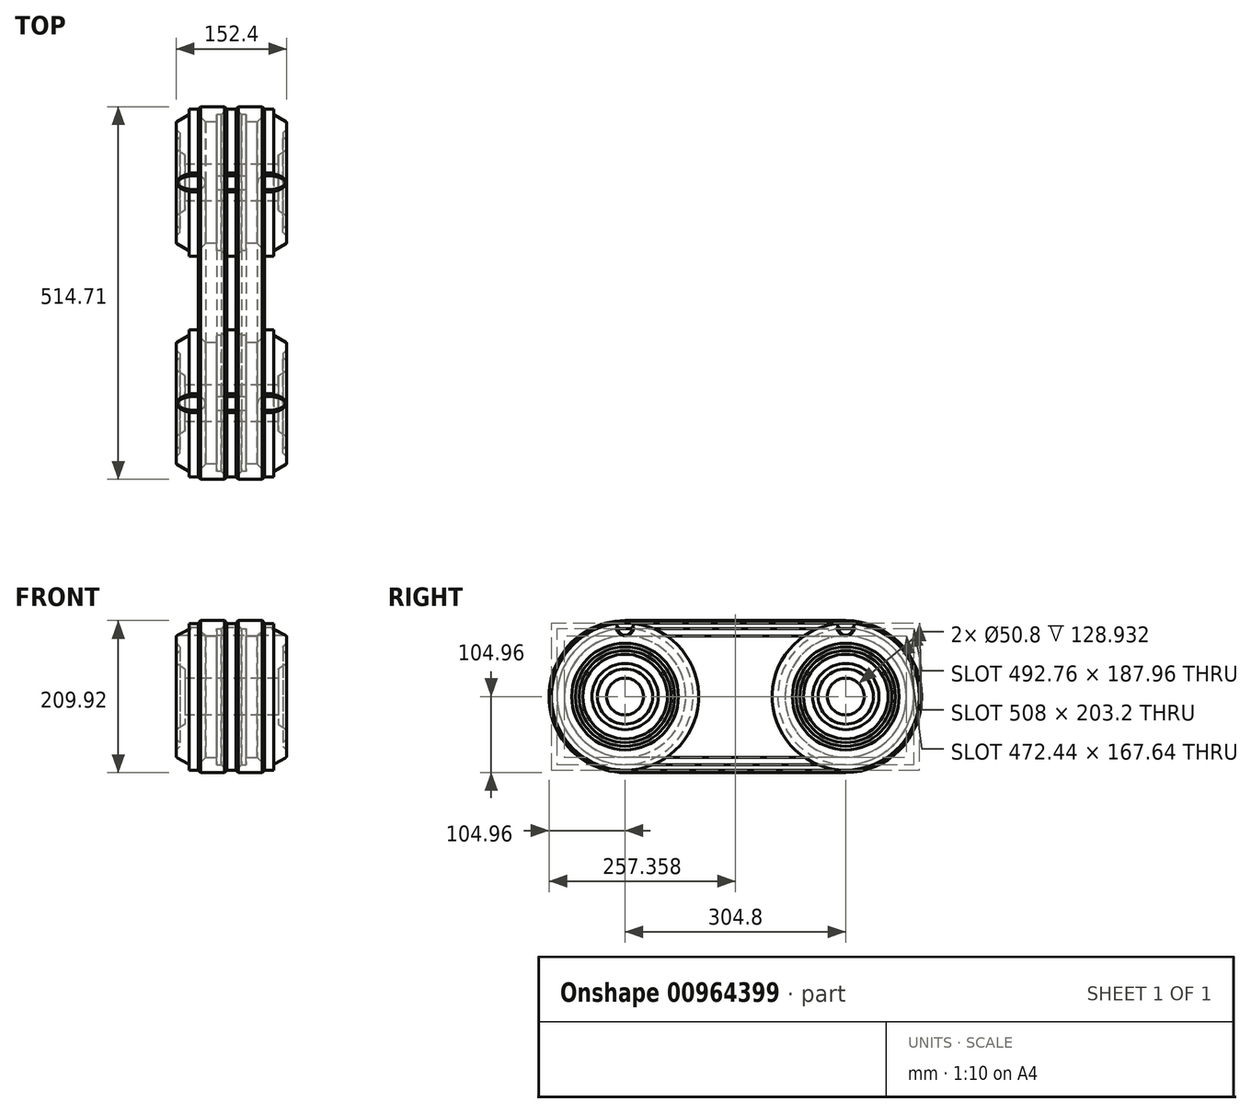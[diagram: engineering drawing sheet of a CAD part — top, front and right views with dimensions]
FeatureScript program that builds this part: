
annotation { "Feature Type Name" : "Feature", "Feature Type Description" : "" }
export const myFeature = defineFeature(function(context is Context, id is Id, definition is map)
    precondition{}
    {
        {
            var Q0;
            Q0=qCreatedBy(makeId("Top.planeOp"),FACE);
            var sketch = newSketch(context, id + "F0", { "sketchPlane" : qUnion([Q0])});
            skLineSegment(sketch, "E0", {"start": v(-162.42, 0) * mm, "end": v(162.97, 0) * mm, "construction": true});
            skLineSegment(sketch, "E1", {"start": v(0, 108.88) * mm, "end": v(0, -100.36) * mm, "construction": true});
            skLineSegment(sketch, "E2", {"start": v(-64.47, 25.4) * mm, "end": v(-64.47, 38.1) * mm});
            skLineSegment(sketch, "E3", {"start": v(-64.47, 38.1) * mm, "end": v(-76.2, 45.72) * mm});
            skLineSegment(sketch, "E4", {"start": v(-76.2, 45.72) * mm, "end": v(-76.2, 58.42) * mm});
            skLineSegment(sketch, "E5", {"start": v(-76.2, 58.42) * mm, "end": v(-71.12, 63.5) * mm});
            skLineSegment(sketch, "E6", {"start": v(-71.12, 63.5) * mm, "end": v(-71.12, 68.58) * mm});
            skLineSegment(sketch, "E7", {"start": v(-71.12, 68.58) * mm, "end": v(-76.2, 73.66) * mm});
            skLineSegment(sketch, "E8", {"start": v(-76.2, 73.66) * mm, "end": v(-76.2, 83.82) * mm});
            skLineSegment(sketch, "E9", {"start": v(-76.2, 83.82) * mm, "end": v(-58.42, 93.98) * mm});
            skLineSegment(sketch, "E10", {"start": v(-58.42, 93.98) * mm, "end": v(-58.42, 101.6) * mm});
            skLineSegment(sketch, "E11", {"start": v(-58.42, 101.6) * mm, "end": v(-45.72, 101.6) * mm});
            skLineSegment(sketch, "E12", {"start": v(-45.72, 101.6) * mm, "end": v(-45.72, 93.98) * mm});
            skLineSegment(sketch, "E13", {"start": v(-45.72, 93.98) * mm, "end": v(-35.56, 83.82) * mm});
            skLineSegment(sketch, "E14", {"start": v(-35.56, 83.82) * mm, "end": v(-20.32, 83.82) * mm});
            skLineSegment(sketch, "E15", {"start": v(-20.32, 83.82) * mm, "end": v(-20.32, 93.98) * mm});
            skLineSegment(sketch, "E16", {"start": v(-20.32, 93.98) * mm, "end": v(-13.97, 93.98) * mm});
            skLineSegment(sketch, "E17", {"start": v(-13.97, 93.98) * mm, "end": v(-6.35, 101.6) * mm});
            skLineSegment(sketch, "E18", {"start": v(-6.35, 101.6) * mm, "end": v(6.35, 101.6) * mm});
            skLineSegment(sketch, "E19", {"start": v(6.35, 101.6) * mm, "end": v(13.97, 93.98) * mm});
            skLineSegment(sketch, "E20", {"start": v(13.97, 93.98) * mm, "end": v(20.32, 93.98) * mm});
            skLineSegment(sketch, "E21", {"start": v(20.32, 93.98) * mm, "end": v(20.32, 83.82) * mm});
            skLineSegment(sketch, "E22", {"start": v(20.32, 83.82) * mm, "end": v(35.56, 83.82) * mm});
            skLineSegment(sketch, "E23", {"start": v(35.56, 83.82) * mm, "end": v(45.72, 93.98) * mm});
            skLineSegment(sketch, "E24", {"start": v(45.72, 93.98) * mm, "end": v(45.72, 101.6) * mm});
            skLineSegment(sketch, "E25", {"start": v(45.72, 101.6) * mm, "end": v(58.42, 101.6) * mm});
            skLineSegment(sketch, "E26", {"start": v(58.42, 101.6) * mm, "end": v(58.42, 93.98) * mm});
            skLineSegment(sketch, "E27", {"start": v(58.42, 93.98) * mm, "end": v(76.2, 83.82) * mm});
            skLineSegment(sketch, "E28", {"start": v(76.2, 83.82) * mm, "end": v(76.2, 73.66) * mm});
            skLineSegment(sketch, "E29", {"start": v(76.2, 73.66) * mm, "end": v(71.12, 68.58) * mm});
            skLineSegment(sketch, "E30", {"start": v(71.12, 68.58) * mm, "end": v(71.12, 63.5) * mm});
            skLineSegment(sketch, "E31", {"start": v(71.12, 63.5) * mm, "end": v(76.2, 58.42) * mm});
            skLineSegment(sketch, "E32", {"start": v(76.2, 58.42) * mm, "end": v(76.2, 45.72) * mm});
            skLineSegment(sketch, "E33", {"start": v(76.2, 45.72) * mm, "end": v(64.47, 38.1) * mm});
            skLineSegment(sketch, "E34", {"start": v(64.47, 38.1) * mm, "end": v(64.47, 25.4) * mm});
            skLineSegment(sketch, "E35", {"start": v(64.47, 25.4) * mm, "end": v(-64.47, 25.4) * mm});
            skSolve(sketch);
        }
        {
            var Q0;
            Q0=makeQuery(id+"F0.imprint","IMPRINT",FACE,{"disambiguationData":[TD([[makeQuery(id+"F0.imprint","IMPRINT",EDGE,{"derivedFrom":sQuery(id+"F0.wireOp",EDGE,"E2")}),-1.0]])]});
            var Q1;
            Q1=sQuery(id+"F0.wireOp",EDGE,"E0");
            revolve(context, id + "F1", {"surfaceOperationType" : NewSurfaceOperationType.NEW, "entities" : qUnion([Q0]), "axis" : qUnion([Q1]), "revolveType" : RevolveType.FULL});
        }
        {
            var Q0;
            Q0=qCreatedBy(makeId("Right.planeOp"),FACE);
            var sketch = newSketch(context, id + "F2", { "sketchPlane" : qUnion([Q0])});
            skCircle(sketch, "E36", {"center": v(0, 0) * mm, "radius": 94.18 * mm, "construction": true});
            skCircle(sketch, "E37", {"center": v(0, 94.18) * mm, "radius": 9.58 * mm});
            skLineSegment(sketch, "E38", {"start": v(9.51, 95.36) * mm, "end": v(16.3, 105.7) * mm});
            skLineSegment(sketch, "E39", {"start": v(16.3, 105.7) * mm, "end": v(-15.78, 105.7) * mm});
            skLineSegment(sketch, "E40", {"start": v(-15.78, 105.7) * mm, "end": v(-9.51, 95.36) * mm});
            skSolve(sketch);
        }
        {
            var Q0;
            Q0 = qSketchRegion(id + "F2", true);
            extrude(context, id + "F3", {"entities" : qUnion([Q0]), "operationType" : NewBodyOperationType.REMOVE, "endBound" : BoundingType.SYMMETRIC, "oppositeDirection" : true, "depth" : 254 * mm, "offsetDistance" : 25.4 * mm});
        }
        {
            var Q0;
            Q0=qCreatedBy(makeId("Top.planeOp"),FACE);
            var sketch = newSketch(context, id + "F4", { "sketchPlane" : qUnion([Q0])});
            skLineSegment(sketch, "E41", {"start": v(-162.42, 0) * mm, "end": v(162.97, 0) * mm, "construction": true});
            skLineSegment(sketch, "E42.MirrorCS", {"start": v(-6.35, -104.96) * mm, "end": v(-45.72, -104.96) * mm});
            skLineSegment(sketch, "E43.MirrorCS", {"start": v(6.35, -101.6) * mm, "end": v(6.35, -104.96) * mm});
            skLineSegment(sketch, "E44.MirrorCS", {"start": v(-6.35, -101.6) * mm, "end": v(-6.35, -104.96) * mm});
            skLineSegment(sketch, "E45.MirrorCS", {"start": v(-20.32, -93.98) * mm, "end": v(-13.97, -93.98) * mm});
            skLineSegment(sketch, "E46.MirrorCS", {"start": v(-45.72, -104.96) * mm, "end": v(-45.72, -101.6) * mm});
            skLineSegment(sketch, "E47.MirrorCS", {"start": v(13.97, -93.98) * mm, "end": v(20.32, -93.98) * mm});
            skLineSegment(sketch, "E48.MirrorCS", {"start": v(45.72, -104.96) * mm, "end": v(45.72, -101.6) * mm});
            skLineSegment(sketch, "E49.MirrorCS", {"start": v(45.72, -93.98) * mm, "end": v(45.72, -101.6) * mm});
            skLineSegment(sketch, "E50.MirrorCS", {"start": v(-45.72, -101.6) * mm, "end": v(-45.72, -93.98) * mm});
            skLineSegment(sketch, "E51.MirrorCS", {"start": v(20.32, -83.82) * mm, "end": v(35.56, -83.82) * mm});
            skLineSegment(sketch, "E52.MirrorCS", {"start": v(-45.72, -93.98) * mm, "end": v(-35.56, -83.82) * mm});
            skLineSegment(sketch, "E53.MirrorCS", {"start": v(-13.97, -93.98) * mm, "end": v(-6.35, -101.6) * mm});
            skLineSegment(sketch, "E54.MirrorCS", {"start": v(6.35, -101.6) * mm, "end": v(13.97, -93.98) * mm});
            skLineSegment(sketch, "E55.MirrorCS", {"start": v(35.56, -83.82) * mm, "end": v(45.72, -93.98) * mm});
            skLineSegment(sketch, "E56.MirrorCS", {"start": v(20.32, -93.98) * mm, "end": v(20.32, -83.82) * mm});
            skLineSegment(sketch, "E57.MirrorCS", {"start": v(-20.32, -83.82) * mm, "end": v(-20.32, -93.98) * mm});
            skLineSegment(sketch, "E58.MirrorCS", {"start": v(6.35, -104.96) * mm, "end": v(45.72, -104.96) * mm});
            skLineSegment(sketch, "E59.MirrorCS", {"start": v(-35.56, -83.82) * mm, "end": v(-20.32, -83.82) * mm});
            skLineSegment(sketch, "E60.MirrorCS", {"start": v(-6.35, -104.96) * mm, "end": v(6.35, -104.96) * mm, "construction": true});
            skSolve(sketch);
        }
        {
            var Q0;
            Q0=qCreatedBy(makeId("Right.planeOp"),FACE);
            var sketch = newSketch(context, id + "F5", { "sketchPlane" : qUnion([Q0])});
            skArc(sketch, "E61", {"start": v(304.8, -104.95) * mm, "mid": v(409.75, 0) * mm, "end": v(304.8, 104.95) * mm});
            skLineSegment(sketch, "E62", {"start": v(0, 104.96) * mm, "end": v(304.8, 104.95) * mm});
            skLineSegment(sketch, "E63", {"start": v(304.8, -104.95) * mm, "end": v(0, -104.96) * mm});
            skArc(sketch, "E64", {"start": v(0, 104.96) * mm, "mid": v(-104.96, 0) * mm, "end": v(0, -104.96) * mm});
            skLineSegment(sketch, "E65", {"start": v(0, 0) * mm, "end": v(304.8, 0) * mm, "construction": true});
            skSolve(sketch);
        }
        {
            var Q0;
            Q0=makeQuery(id+"F4.imprint","IMPRINT",FACE,{"disambiguationData":[TD([[makeQuery(id+"F4.imprint","IMPRINT",EDGE,{"derivedFrom":sQuery(id+"F4.wireOp",EDGE,"E43.MirrorCS")}),1.0]])]});
            var Q1;
            Q1=makeQuery(id+"F4.imprint","IMPRINT",FACE,{"disambiguationData":[TD([[makeQuery(id+"F4.imprint","IMPRINT",EDGE,{"derivedFrom":sQuery(id+"F4.wireOp",EDGE,"E44.MirrorCS")}),-1.0]])]});
            var Q2;
            Q2=sQuery(id+"F5.wireOp",EDGE,"E62");
            var Q3;
            Q3=sQuery(id+"F5.wireOp",EDGE,"E64");
            var Q4;
            Q4=sQuery(id+"F5.wireOp",EDGE,"E61");
            var Q5;
            Q5=sQuery(id+"F5.wireOp",EDGE,"E63");
            sweep(context, id + "F6", {"profiles" : qUnion([Q0, Q1]), "path" : qUnion([Q2, Q3, Q4, Q5])});
        }
        {
            var Q0;
            Q0=makeQuery(id+"F1.opRevolve","SWEPT_BODY",BODY,{"disambiguationData":[OSD([sQuery(id+"F0.wireOp",EDGE,"E2"),sQuery(id+"F0.wireOp",EDGE,"E3"),sQuery(id+"F0.wireOp",EDGE,"E4"),sQuery(id+"F0.wireOp",EDGE,"E5"),sQuery(id+"F0.wireOp",EDGE,"E6"),sQuery(id+"F0.wireOp",EDGE,"E7"),sQuery(id+"F0.wireOp",EDGE,"E8"),sQuery(id+"F0.wireOp",EDGE,"E9"),sQuery(id+"F0.wireOp",EDGE,"E10"),sQuery(id+"F0.wireOp",EDGE,"E11"),sQuery(id+"F0.wireOp",EDGE,"E12"),sQuery(id+"F0.wireOp",EDGE,"E13"),sQuery(id+"F0.wireOp",EDGE,"E14"),sQuery(id+"F0.wireOp",EDGE,"E15"),sQuery(id+"F0.wireOp",EDGE,"E16"),sQuery(id+"F0.wireOp",EDGE,"E17"),sQuery(id+"F0.wireOp",EDGE,"E18"),sQuery(id+"F0.wireOp",EDGE,"E19"),sQuery(id+"F0.wireOp",EDGE,"E20"),sQuery(id+"F0.wireOp",EDGE,"E21"),sQuery(id+"F0.wireOp",EDGE,"E22"),sQuery(id+"F0.wireOp",EDGE,"E23"),sQuery(id+"F0.wireOp",EDGE,"E24"),sQuery(id+"F0.wireOp",EDGE,"E25"),sQuery(id+"F0.wireOp",EDGE,"E26"),sQuery(id+"F0.wireOp",EDGE,"E27"),sQuery(id+"F0.wireOp",EDGE,"E28"),sQuery(id+"F0.wireOp",EDGE,"E29"),sQuery(id+"F0.wireOp",EDGE,"E30"),sQuery(id+"F0.wireOp",EDGE,"E31"),sQuery(id+"F0.wireOp",EDGE,"E32"),sQuery(id+"F0.wireOp",EDGE,"E33"),sQuery(id+"F0.wireOp",EDGE,"E34"),sQuery(id+"F0.wireOp",EDGE,"E35")])]});
            var Q1;
            Q1=sQuery(id+"F5.wireOp",EDGE,"E65");
            transform(context, id + "F7", {"entities" : qUnion([Q0]), "transformType" : TransformType.TRANSLATION_ENTITY, "oppositeDirectionEntity" : false, "transformLine" : qUnion([Q1]), "makeCopy" : true});
        }
        {
            var Q0;
            Q0=makeQuery(id+"F6.opSweep","SWEPT_EDGE",EDGE,{"disambiguationData":[OSD([sQuery(id+"F4.wireOp",EDGE,"E48.MirrorCS"),sQuery(id+"F4.wireOp",EDGE,"E58.MirrorCS"),sQuery(id+"F5.wireOp",EDGE,"E62")])]});
            var Q1;
            Q1=makeQuery(id+"F6.opSweep","SWEPT_FACE",FACE,{"disambiguationData":[OSD([sQuery(id+"F4.wireOp",EDGE,"E58.MirrorCS"),sQuery(id+"F5.wireOp",EDGE,"E62")])]});
            var Q2;
            Q2=makeQuery(id+"F6.opSweep","SWEPT_FACE",FACE,{"disambiguationData":[OSD([sQuery(id+"F4.wireOp",EDGE,"E58.MirrorCS"),sQuery(id+"F5.wireOp",EDGE,"E64")])]});
            var Q3;
            Q3=makeQuery(id+"F6.opSweep","SWEPT_FACE",FACE,{"disambiguationData":[OSD([sQuery(id+"F4.wireOp",EDGE,"E58.MirrorCS"),sQuery(id+"F5.wireOp",EDGE,"E61")])]});
            var Q4;
            Q4=makeQuery(id+"F6.opSweep","SWEPT_FACE",FACE,{"disambiguationData":[OSD([sQuery(id+"F4.wireOp",EDGE,"E58.MirrorCS"),sQuery(id+"F5.wireOp",EDGE,"E63")])]});
            var Q5;
            Q5=makeQuery(id+"F6.opSweep","SWEPT_FACE",FACE,{"disambiguationData":[OSD([sQuery(id+"F4.wireOp",EDGE,"E42.MirrorCS"),sQuery(id+"F5.wireOp",EDGE,"E64")])]});
            var Q6;
            Q6=makeQuery(id+"F6.opSweep","SWEPT_FACE",FACE,{"disambiguationData":[OSD([sQuery(id+"F4.wireOp",EDGE,"E42.MirrorCS"),sQuery(id+"F5.wireOp",EDGE,"E63")])]});
            var Q7;
            Q7=makeQuery(id+"F6.opSweep","SWEPT_FACE",FACE,{"disambiguationData":[OSD([sQuery(id+"F4.wireOp",EDGE,"E42.MirrorCS"),sQuery(id+"F5.wireOp",EDGE,"E62")])]});
            chamfer(context, id + "F8", {"entities" : qUnion([Q0, Q1, Q2, Q3, Q4, Q5, Q6, Q7]), "width" : 3.3 * mm, "tangentPropagation" : true});
        }
        {
            var Q0;
            Q0=makeQuery(id+"F7.opPattern","COPY",FACE,{"derivedFrom":makeQuery(id+"F1.opRevolve","SWEPT_FACE",FACE,{"disambiguationData":[OSD([sQuery(id+"F0.wireOp",EDGE,"E9")])]}),"instanceName":"1"});
            var Q1;
            Q1=makeQuery(id+"F7.opPattern","COPY",FACE,{"derivedFrom":makeQuery(id+"F1.opRevolve","SWEPT_FACE",FACE,{"disambiguationData":[OSD([sQuery(id+"F0.wireOp",EDGE,"E27")])]}),"instanceName":"1"});
            var Q2;
            Q2=makeQuery(id+"F1.opRevolve","SWEPT_FACE",FACE,{"disambiguationData":[OSD([sQuery(id+"F0.wireOp",EDGE,"E27")])]});
            var Q3;
            Q3=makeQuery(id+"F1.opRevolve","SWEPT_FACE",FACE,{"disambiguationData":[OSD([sQuery(id+"F0.wireOp",EDGE,"E9")])]});
            fillet(context, id + "F9", {"entities" : qUnion([Q0, Q1, Q2, Q3]), "radius" : 2.54 * mm, "tangentPropagation" : true, "allowEdgeOverflow" : false});
        }
    });
